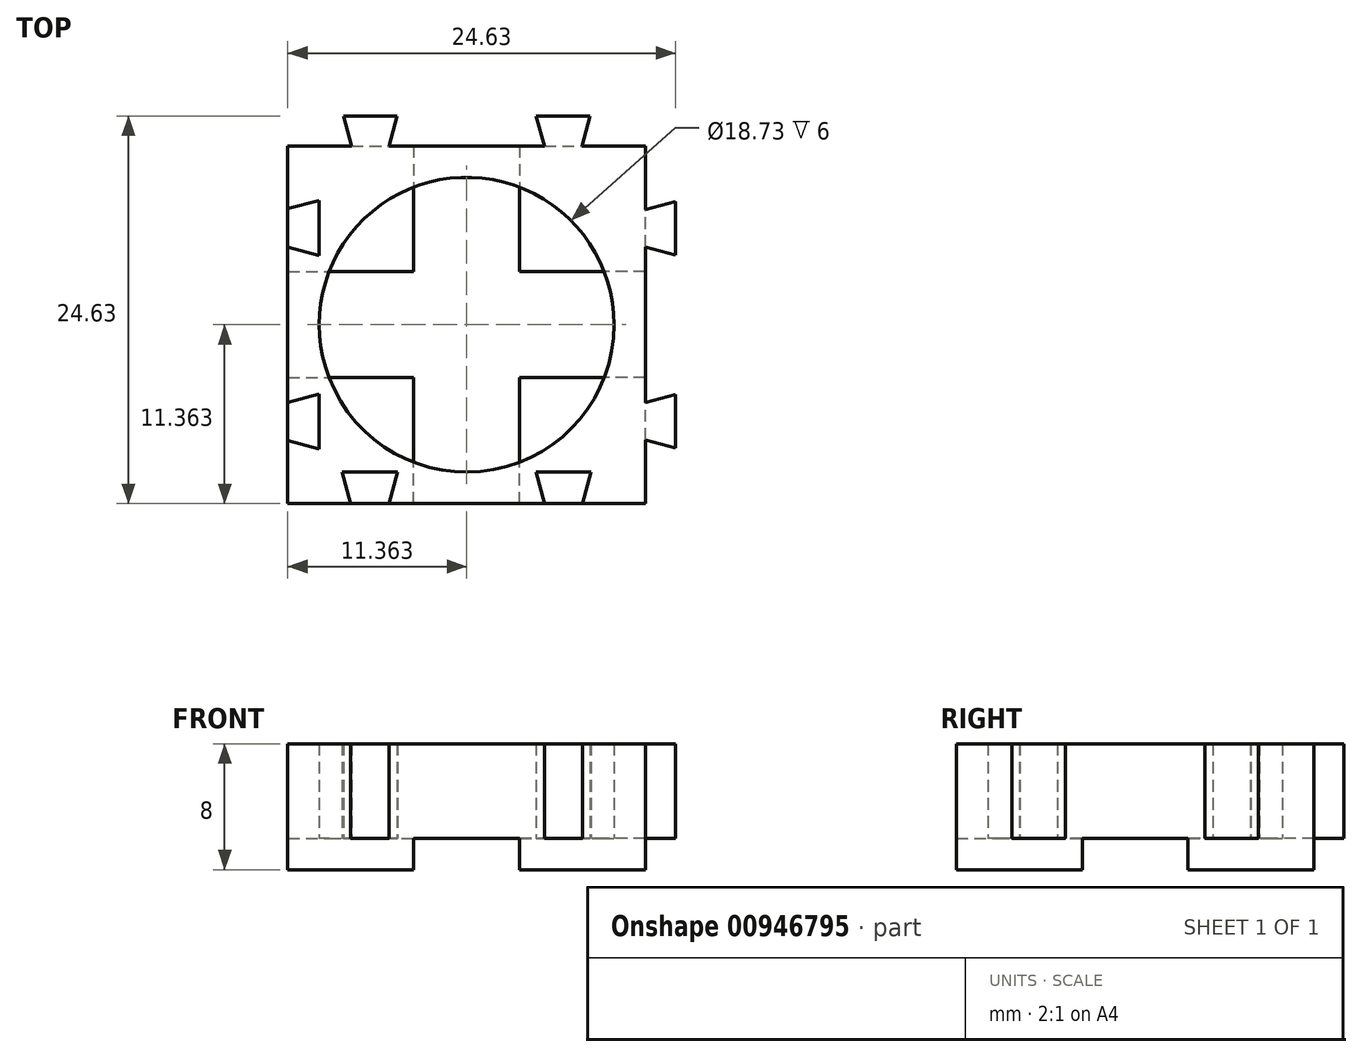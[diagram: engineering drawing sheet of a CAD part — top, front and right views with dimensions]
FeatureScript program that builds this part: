
annotation { "Feature Type Name" : "Feature", "Feature Type Description" : "" }
export const myFeature = defineFeature(function(context is Context, id is Id, definition is map)
    precondition{}
    {
        {
            var Q0;
            Q0=qCreatedBy(makeId("Top.planeOp"),FACE);
            var sketch = newSketch(context, id + "F0", { "sketchPlane" : qUnion([Q0])});
            skLineSegment(sketch, "E0.bottom", {"start": v(0, 0) * mm, "end": v(4, 0) * mm});
            skLineSegment(sketch, "E0.top", {"start": v(0, 22.73) * mm, "end": v(22.73, 22.73) * mm});
            skLineSegment(sketch, "E0.left", {"start": v(0, 0) * mm, "end": v(0, 4) * mm});
            skLineSegment(sketch, "E0.right", {"start": v(22.73, 0) * mm, "end": v(22.73, 22.73) * mm});
            skLineSegment(sketch, "E1", {"start": v(0, 0) * mm, "end": v(22.73, 22.73) * mm, "construction": true});
            skLineSegment(sketch, "E2", {"start": v(0, 22.73) * mm, "end": v(22.73, 0) * mm, "construction": true});
            skCircle(sketch, "E3", {"center": v(11.36, 11.36) * mm, "radius": 9.36 * mm});
            skLineSegment(sketch, "E4", {"start": v(4, 0) * mm, "end": v(3.46, 2) * mm});
            skLineSegment(sketch, "E5", {"start": v(3.46, 2) * mm, "end": v(6.96, 2) * mm});
            skLineSegment(sketch, "E6", {"start": v(6.96, 2) * mm, "end": v(6.43, 0) * mm});
            skLineSegment(sketch, "E7.trimOffspring", {"start": v(6.43, 0) * mm, "end": v(16.3, 0) * mm});
            skLineSegment(sketch, "E8", {"start": v(11.36, 22.73) * mm, "end": v(11.36, 0) * mm, "construction": true});
            skLineSegment(sketch, "E9.MirrorCS", {"start": v(15.76, 2) * mm, "end": v(16.3, 0) * mm});
            skLineSegment(sketch, "E10.MirrorCS", {"start": v(19.26, 2) * mm, "end": v(15.76, 2) * mm});
            skLineSegment(sketch, "E11.MirrorCS", {"start": v(18.73, 0) * mm, "end": v(19.26, 2) * mm});
            skLineSegment(sketch, "E12.trimOffspring", {"start": v(18.73, 0) * mm, "end": v(22.73, 0) * mm});
            skLineSegment(sketch, "E13.MirrorCS", {"start": v(2, 15.76) * mm, "end": v(0, 16.3) * mm});
            skLineSegment(sketch, "E14.MirrorCS", {"start": v(0, 18.73) * mm, "end": v(2, 19.26) * mm});
            skLineSegment(sketch, "E15.MirrorCS", {"start": v(2, 19.26) * mm, "end": v(2, 15.76) * mm});
            skLineSegment(sketch, "E16.MirrorCS", {"start": v(0, 4) * mm, "end": v(2, 3.46) * mm});
            skLineSegment(sketch, "E17.MirrorCS", {"start": v(2, 3.46) * mm, "end": v(2, 6.96) * mm});
            skLineSegment(sketch, "E18.MirrorCS", {"start": v(2, 6.96) * mm, "end": v(0, 6.43) * mm});
            skLineSegment(sketch, "E19.trimOffspring", {"start": v(0, 18.73) * mm, "end": v(0, 22.73) * mm});
            skLineSegment(sketch, "E20.trimOffspring", {"start": v(0, 6.43) * mm, "end": v(0, 16.3) * mm});
            skLineSegment(sketch, "E21", {"start": v(22.73, 4.05) * mm, "end": v(24.63, 3.54) * mm});
            skLineSegment(sketch, "E22", {"start": v(24.63, 3.54) * mm, "end": v(24.63, 6.94) * mm});
            skLineSegment(sketch, "E23", {"start": v(24.63, 6.94) * mm, "end": v(22.73, 6.43) * mm});
            skLineSegment(sketch, "E24", {"start": v(0, 11.36) * mm, "end": v(22.73, 11.36) * mm, "construction": true});
            skLineSegment(sketch, "E25.MirrorCS", {"start": v(22.73, 18.68) * mm, "end": v(24.63, 19.18) * mm});
            skLineSegment(sketch, "E26.MirrorCS", {"start": v(24.63, 19.18) * mm, "end": v(24.63, 15.78) * mm});
            skLineSegment(sketch, "E27.MirrorCS", {"start": v(24.63, 15.78) * mm, "end": v(22.73, 16.3) * mm});
            skLineSegment(sketch, "E28.MirrorCS", {"start": v(19.18, 24.63) * mm, "end": v(15.78, 24.63) * mm});
            skLineSegment(sketch, "E29.MirrorCS", {"start": v(18.68, 22.73) * mm, "end": v(19.18, 24.63) * mm});
            skLineSegment(sketch, "E30.MirrorCS", {"start": v(4.05, 22.73) * mm, "end": v(3.54, 24.63) * mm});
            skLineSegment(sketch, "E31.MirrorCS", {"start": v(15.78, 24.63) * mm, "end": v(16.3, 22.73) * mm});
            skLineSegment(sketch, "E32.MirrorCS", {"start": v(6.94, 24.63) * mm, "end": v(6.43, 22.73) * mm});
            skLineSegment(sketch, "E33.MirrorCS", {"start": v(3.54, 24.63) * mm, "end": v(6.94, 24.63) * mm});
            skSolve(sketch);
        }
        {
            var Q0;
            Q0 = qSketchRegion(id + "F0", true);
            extrude(context, id + "F1", {"entities" : qUnion([Q0]), "depth" : 6 * mm, "offsetDistance" : 25 * mm});
        }
        {
            var Q0;
            Q0=makeQuery(id+"F1.opExtrude","CAP_FACE",FACE,{"disambiguationData":[OSD([sQuery(id+"F0.wireOp",EDGE,"E0.bottom"),sQuery(id+"F0.wireOp",EDGE,"E0.top"),sQuery(id+"F0.wireOp",EDGE,"E0.left"),sQuery(id+"F0.wireOp",EDGE,"E0.right"),sQuery(id+"F0.wireOp",EDGE,"E3")])],"isStart":true});
            var sketch = newSketch(context, id + "F2", { "sketchPlane" : qUnion([Q0])});
            skLineSegment(sketch, "E34.bottom", {"start": v(0, 0) * mm, "end": v(8, 0) * mm});
            skLineSegment(sketch, "E34.top", {"start": v(0, -8) * mm, "end": v(8, -8) * mm});
            skLineSegment(sketch, "E34.left", {"start": v(0, 0) * mm, "end": v(0, -8) * mm});
            skLineSegment(sketch, "E34.right", {"start": v(8, 0) * mm, "end": v(8, -8) * mm});
            skLineSegment(sketch, "E35", {"start": v(0, -11.36) * mm, "end": v(22.73, -11.36) * mm, "construction": true});
            skLineSegment(sketch, "E36.MirrorCS", {"start": v(0, -22.73) * mm, "end": v(0, -14.73) * mm});
            skLineSegment(sketch, "E37.MirrorCS", {"start": v(0, -14.73) * mm, "end": v(8, -14.73) * mm});
            skLineSegment(sketch, "E38.MirrorCS", {"start": v(0, -22.73) * mm, "end": v(8, -22.73) * mm});
            skLineSegment(sketch, "E39.MirrorCS", {"start": v(8, -22.73) * mm, "end": v(8, -14.73) * mm});
            skLineSegment(sketch, "E40", {"start": v(11.36, -22.73) * mm, "end": v(11.36, 0) * mm, "construction": true});
            skLineSegment(sketch, "E41.MirrorCS", {"start": v(22.73, -14.73) * mm, "end": v(14.73, -14.73) * mm});
            skLineSegment(sketch, "E42.MirrorCS", {"start": v(14.73, -22.73) * mm, "end": v(14.73, -14.73) * mm});
            skLineSegment(sketch, "E43.MirrorCS", {"start": v(22.73, -22.73) * mm, "end": v(22.73, -14.73) * mm});
            skLineSegment(sketch, "E44.MirrorCS", {"start": v(22.73, -22.73) * mm, "end": v(14.73, -22.73) * mm});
            skLineSegment(sketch, "E45.MirrorCS", {"start": v(22.73, 0) * mm, "end": v(22.73, -8) * mm});
            skLineSegment(sketch, "E46.MirrorCS", {"start": v(22.73, 0) * mm, "end": v(14.73, 0) * mm});
            skLineSegment(sketch, "E47.MirrorCS", {"start": v(22.73, -8) * mm, "end": v(14.73, -8) * mm});
            skLineSegment(sketch, "E48.MirrorCS", {"start": v(14.73, 0) * mm, "end": v(14.73, -8) * mm});
            skSolve(sketch);
        }
        {
            var Q0;
            Q0 = qSketchRegion(id + "F2", true);
            extrude(context, id + "F3", {"entities" : qUnion([Q0]), "operationType" : NewBodyOperationType.ADD, "depth" : 2 * mm, "offsetDistance" : 25 * mm});
        }
    });
